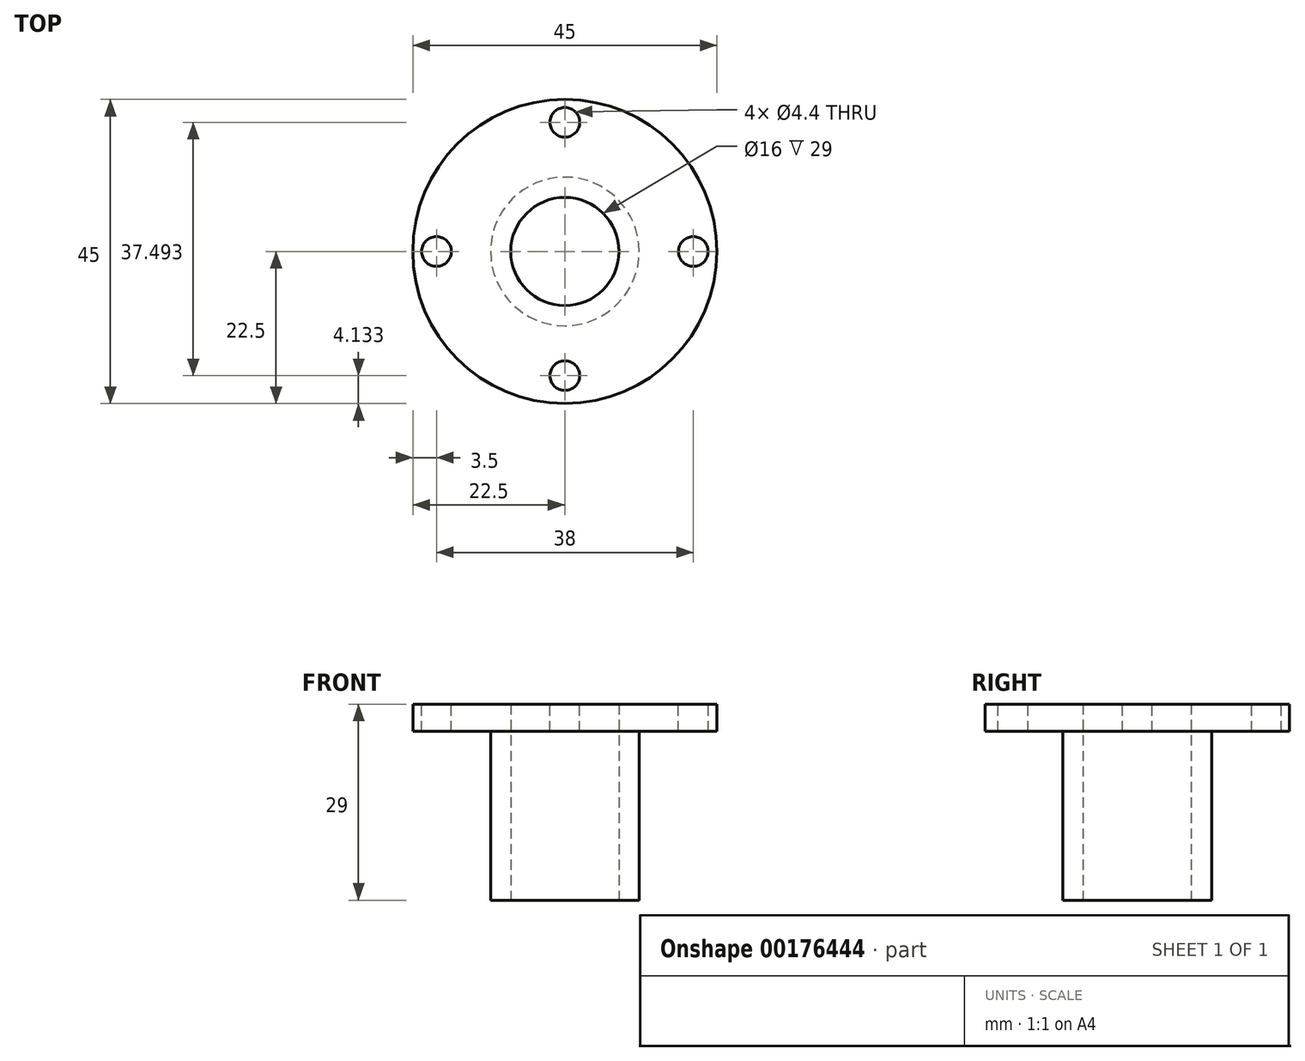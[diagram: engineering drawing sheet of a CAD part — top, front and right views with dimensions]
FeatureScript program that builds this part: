
annotation { "Feature Type Name" : "Feature", "Feature Type Description" : "" }
export const myFeature = defineFeature(function(context is Context, id is Id, definition is map)
    precondition{}
    {
        {
            var Q0;
            Q0=qCreatedBy(makeId("Top.planeOp"),FACE);
            var sketch = newSketch(context, id + "F0", { "sketchPlane" : qUnion([Q0])});
            skCircle(sketch, "E0", {"center": v(0, 0) * mm, "radius": 11 * mm});
            skCircle(sketch, "E1", {"center": v(0, 0) * mm, "radius": 8 * mm});
            skSolve(sketch);
        }
        {
            var Q0;
            Q0=makeQuery(id+"F0.imprint","IMPRINT",FACE,{"disambiguationData":[TD([[makeQuery(id+"F0.imprint","IMPRINT",EDGE,{"derivedFrom":sQuery(id+"F0.wireOp",EDGE,"E0")}),1.0]])]});
            extrude(context, id + "F1", {"entities" : qUnion([Q0]), "depth" : 25 * mm});
        }
        {
            var Q0;
            Q0=makeQuery(id+"F1.opExtrude","CAP_FACE",FACE,{"disambiguationData":[OSD([sQuery(id+"F0.wireOp",EDGE,"E0"),sQuery(id+"F0.wireOp",EDGE,"E1")])],"isStart":false});
            var sketch = newSketch(context, id + "F2", { "sketchPlane" : qUnion([Q0])});
            skCircle(sketch, "E2", {"center": v(0, 0) * mm, "radius": 22.5 * mm});
            skSolve(sketch);
        }
        {
            var Q0;
            Q0=makeQuery(id+"F2.imprint","IMPRINT",FACE,{"disambiguationData":[TD([[makeQuery(id+"F2.imprint","IMPRINT",EDGE,{"derivedFrom":sQuery(id+"F2.wireOp",EDGE,"E2")}),1.0]])]});
            var Q1;
            Q1=makeQuery(id+"F2.imprint","IMPRINT",FACE,{"disambiguationData":[TD([[makeQuery(id+"F2.imprint","IMPRINT",EDGE,{"derivedFrom":makeQuery(id+"F1.opExtrude","CAP_EDGE",EDGE,{"disambiguationData":[OSD([sQuery(id+"F0.wireOp",EDGE,"E0")])],"isStart":false})}),1.0]])]});
            extrude(context, id + "F3", {"entities" : qUnion([Q0, Q1]), "operationType" : NewBodyOperationType.ADD, "depth" : 4 * mm});
        }
        {
            var Q0;
            Q0=makeQuery(id+"F3.opExtrude","CAP_FACE",FACE,{"disambiguationData":[OSD([sQuery(id+"F0.wireOp",EDGE,"E1"),sQuery(id+"F2.wireOp",EDGE,"E2")])],"isStart":false});
            var sketch = newSketch(context, id + "F4", { "sketchPlane" : qUnion([Q0])});
            skCircle(sketch, "E3", {"center": v(-19, 0) * mm, "radius": 2.05 * mm});
            skCircle(sketch, "E4", {"center": v(19, 0) * mm, "radius": 2.4 * mm});
            skCircle(sketch, "E5", {"center": v(0, -18.37) * mm, "radius": 2.58 * mm});
            skCircle(sketch, "E6", {"center": v(0, 19.13) * mm, "radius": 2.55 * mm});
            skSolve(sketch);
        }
        {
            var Q0;
            Q0=sQuery(id+"F4.wireOp",VERTEX,"E3.center");
            var Q1;
            Q1=sQuery(id+"F4.wireOp",VERTEX,"E6.center");
            var Q2;
            Q2=sQuery(id+"F4.wireOp",VERTEX,"E4.center");
            var Q3;
            Q3=sQuery(id+"F4.wireOp",VERTEX,"E5.center");
            var Q4;
            Q4=makeQuery(id+"F1.opExtrude","SWEPT_BODY",BODY,{"disambiguationData":[OSD([sQuery(id+"F0.wireOp",EDGE,"E0"),sQuery(id+"F0.wireOp",EDGE,"E1")])]});
            hole(context, id + "F5", {"style" : HoleStyle.SIMPLE, "endStyle" : HoleEndStyle.THROUGH, "standardTappedOrClearance" : lookupTablePath({ "standard" : "ISO", "fit" : "Normal", "size" : "M4", "type" : "Clearance" }), "standardBlindInLast" : lookupTablePath({ "fit" : "Standard", "standard" : "ISO", "size" : "M4", "type" : "Clearance" }), "holeDiameter" : 4.4 * mm, "startFromSketch" : true, "locations" : qUnion([Q0, Q1, Q2, Q3]), "scope" : qUnion([Q4]), "isTappedThrough" : true});
        }
    });
